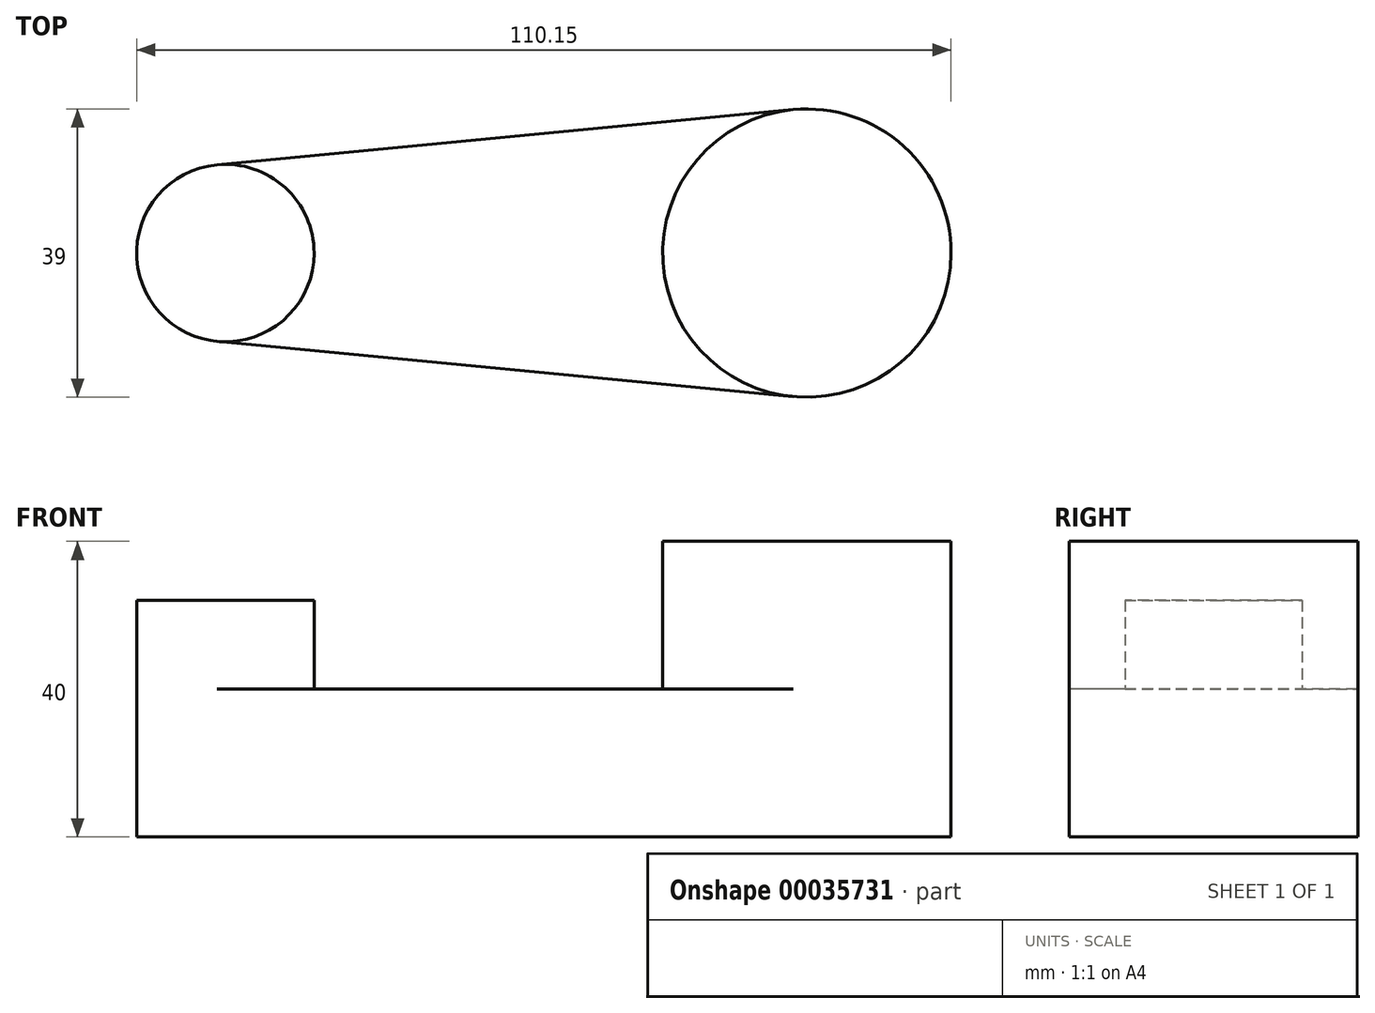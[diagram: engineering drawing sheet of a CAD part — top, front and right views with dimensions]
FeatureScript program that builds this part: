
annotation { "Feature Type Name" : "Feature", "Feature Type Description" : "" }
export const myFeature = defineFeature(function(context is Context, id is Id, definition is map)
    precondition{}
    {
        {
            var Q0;
            Q0=qCreatedBy(makeId("Top.planeOp"),FACE);
            var sketch = newSketch(context, id + "F0", { "sketchPlane" : qUnion([Q0])});
            skArc(sketch, "E0", {"start": v(-1.14, 11.95) * mm, "mid": v(-12, 0) * mm, "end": v(-1.14, -11.95) * mm});
            skArc(sketch, "E1", {"start": v(76.8, -19.41) * mm, "mid": v(98.15, 0) * mm, "end": v(76.8, 19.41) * mm});
            skLineSegment(sketch, "E2", {"start": v(-1.14, 11.95) * mm, "end": v(76.8, 19.41) * mm});
            skLineSegment(sketch, "E3", {"start": v(-1.14, -11.95) * mm, "end": v(76.8, -19.41) * mm});
            skSolve(sketch);
        }
        {
            var Q0;
            Q0=makeQuery(id+"F0.imprint","IMPRINT",FACE,{"disambiguationData":[TD([[makeQuery(id+"F0.imprint","IMPRINT",EDGE,{"derivedFrom":sQuery(id+"F0.wireOp",EDGE,"E0")}),1.0]])]});
            extrude(context, id + "F1", {"entities" : qUnion([Q0]), "depth" : 20 * mm});
        }
        {
            var Q0;
            Q0=makeQuery(id+"F1.opExtrude","CAP_FACE",FACE,{"disambiguationData":[OSD([sQuery(id+"F0.wireOp",EDGE,"E0"),sQuery(id+"F0.wireOp",EDGE,"E1"),sQuery(id+"F0.wireOp",EDGE,"E2"),sQuery(id+"F0.wireOp",EDGE,"E3")])],"isStart":false});
            var sketch = newSketch(context, id + "F2", { "sketchPlane" : qUnion([Q0])});
            skCircle(sketch, "E4", {"center": v(78.65, 0) * mm, "radius": 19.5 * mm});
            skPoint(sketch, "E4.first.point", {"position": v(87.87, 17.18) * mm});
            skPoint(sketch, "E4.second.point", {"position": v(97.76, -3.88) * mm});
            skPoint(sketch, "E4.third.point", {"position": v(79.6, -19.48) * mm});
            skCircle(sketch, "E5", {"center": v(0, 0) * mm, "radius": 12 * mm});
            skPoint(sketch, "E5.first.point", {"position": v(-5.93, 10.43) * mm});
            skPoint(sketch, "E5.second.point", {"position": v(-10.5, -5.82) * mm});
            skPoint(sketch, "E5.third.point", {"position": v(-1.14, -11.95) * mm});
            skSolve(sketch);
        }
        {
            var Q0;
            {var subQ0=sQuery(id+"F2.wireOp",EDGE,"E4");var subQ2=makeQuery(id+"F2.imprint","INTERSECT",VERTEX,{"derivedFrom":[makeQuery(id+"F1.opExtrude","CAP_EDGE",EDGE,{"disambiguationData":[OSD([sQuery(id+"F0.wireOp",EDGE,"E3")])],"isStart":false}),subQ0]});Q0=makeQuery(id+"F2.imprint","IMPRINT",FACE,{"disambiguationData":[TD([[makeQuery(id+"F2.imprint","IMPRINT",EDGE,{"disambiguationData":[TD([[subQ2,-1.0]])],"derivedFrom":subQ0}),1.0]])]});}
            extrude(context, id + "F3", {"entities" : qUnion([Q0]), "operationType" : NewBodyOperationType.ADD, "depth" : 20 * mm});
        }
        {
            var Q0;
            Q0=makeQuery(id+"F1.opExtrude","CAP_FACE",FACE,{"disambiguationData":[OSD([sQuery(id+"F0.wireOp",EDGE,"E0"),sQuery(id+"F0.wireOp",EDGE,"E1"),sQuery(id+"F0.wireOp",EDGE,"E2"),sQuery(id+"F0.wireOp",EDGE,"E3")])],"isStart":false});
            var sketch = newSketch(context, id + "F4", { "sketchPlane" : qUnion([Q0])});
            skCircle(sketch, "E6", {"center": v(0, 0) * mm, "radius": 12 * mm});
            skPoint(sketch, "E6.first.point", {"position": v(-8.3, 8.67) * mm});
            skPoint(sketch, "E6.second.point", {"position": v(-11.41, -3.71) * mm});
            skPoint(sketch, "E6.third.point", {"position": v(-4.34, -11.19) * mm});
            skSolve(sketch);
        }
        {
            var Q0;
            {var subQ0=sQuery(id+"F4.wireOp",EDGE,"E6");var subQ2=makeQuery(id+"F4.imprint","INTERSECT",VERTEX,{"derivedFrom":[makeQuery(id+"F1.opExtrude","CAP_EDGE",EDGE,{"disambiguationData":[OSD([sQuery(id+"F0.wireOp",EDGE,"E2")])],"isStart":false}),subQ0]});Q0=makeQuery(id+"F4.imprint","IMPRINT",FACE,{"disambiguationData":[TD([[makeQuery(id+"F4.imprint","IMPRINT",EDGE,{"disambiguationData":[TD([[subQ2,-1.0]])],"derivedFrom":subQ0}),1.0]])]});}
            extrude(context, id + "F5", {"entities" : qUnion([Q0]), "operationType" : NewBodyOperationType.ADD, "depth" : 12 * mm});
        }
    });
